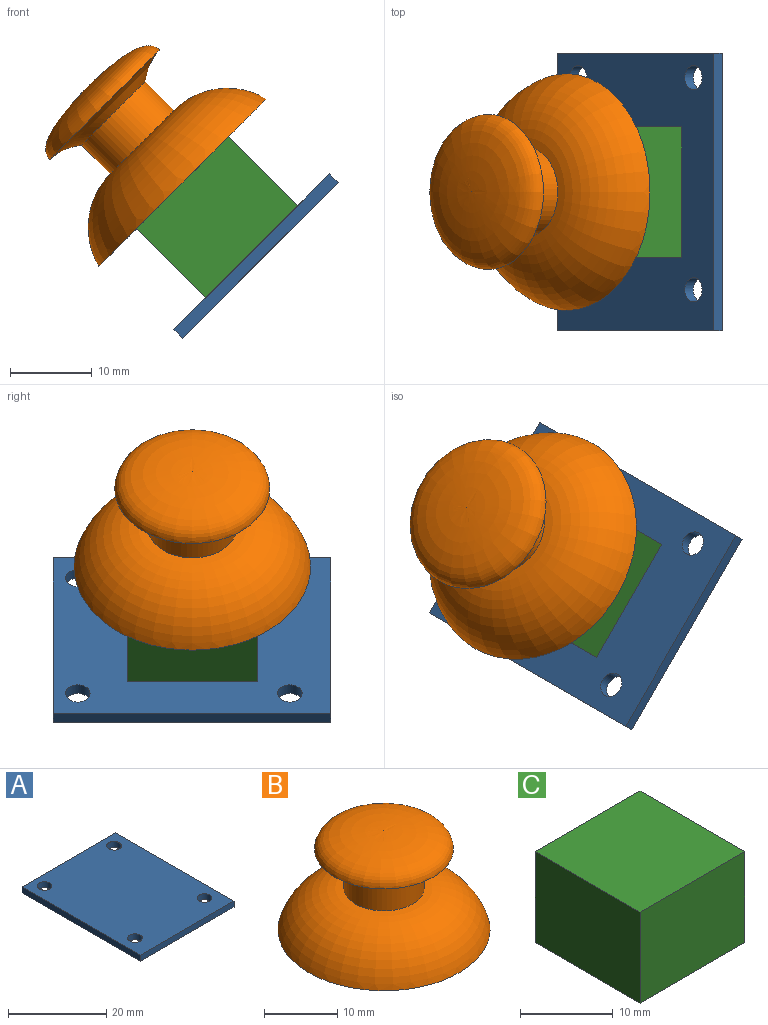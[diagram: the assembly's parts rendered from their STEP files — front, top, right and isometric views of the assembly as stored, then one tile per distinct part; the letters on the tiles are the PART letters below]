
ASSEMBLY  parts=3 mates=2
PART A: 10 faces, bbox 27x34x1.5 mm
  f0: plane 27x1.5mm, normal (0,-1,0), area 40.5mm2, adj f1,f7,f8,f9
  f1: plane 34x1.5mm, normal (1,0,0), area 51mm2, adj f0,f2,f8,f9
  f2: plane 27x1.5mm, normal (0,1,0), area 40.5mm2, adj f1,f7,f8,f9
  f3: cylinder r=1.5mm len=3mm, axis (0,0,-1), area 14.1mm2, adj f8,f9
  f4: cylinder r=1.5mm len=3mm, axis (0,0,-1), area 14.1mm2, adj f8,f9
  f5: cylinder r=1.5mm len=3mm, axis (0,0,-1), area 14.1mm2, adj f8,f9
  f6: cylinder r=1.5mm len=3mm, axis (0,0,-1), area 14.1mm2, adj f8,f9
  f7: plane 34x1.5mm, normal (-1,0,0), area 51mm2, adj f0,f2,f8,f9
  f8: plane 34x27mm, normal (0,0,1), area 889.7mm2, adj f0,f1,f2,f3,f4,f5,f6,f7
  f9: plane 34x27mm, normal (0,0,-1), area 889.7mm2, adj f0,f1,f2,f3,f4,f5,f6,f7
PART B: 5 faces, bbox 29x29x16.5 mm
  f0: revolved ~19x19mm, area 202.8mm2, adj f1,f4
  f1: revolved ~19x19mm, area 351.2mm2, adj f0
  f2: plane 29x29mm, normal (0,0,-1), area 660.5mm2, adj f3
  f3: torus R=5.5mm, axis (0,0,-1), area 832.7mm2, adj f2,f4
  f4: cylinder r=5.5mm len=11mm, axis (0,0,-1), area 172.8mm2, adj f0,f3
PART C: 6 faces, bbox 16x16x12 mm
  f0: plane 16x12mm, normal (0,-1,0), area 192mm2, adj f1,f3,f4,f5
  f1: plane 16x12mm, normal (1,0,0), area 192mm2, adj f0,f2,f4,f5
  f2: plane 16x12mm, normal (0,1,0), area 192mm2, adj f1,f3,f4,f5
  f3: plane 16x12mm, normal (-1,0,0), area 192mm2, adj f0,f2,f4,f5
  f4: plane 16x16mm, normal (0,0,1), area 256mm2, adj f0,f1,f2,f3
  f5: plane 16x16mm, normal (0,0,-1), area 256mm2, adj f0,f1,f2,f3
PLACE A rot(axis=(0,-1,0),45deg) t=(-9.48,-38.97,51.14)mm
PLACE B rot(axis=(0,-1,0),45deg) t=(-50.01,-9.9,29.71)mm
PLACE C rot(axis=(0.92,0,0.38),180deg) t=(-79.27,20.43,0.45)mm
MATE fastened C.f4 <-> A.f8  axis (0.71,0,-0.71) through (-41.52,-9.9,21.22)mm
MATE fastened B.f3 <-> C.f5  axis (0.71,0,-0.71) through (-50.01,-9.9,29.71)mm
